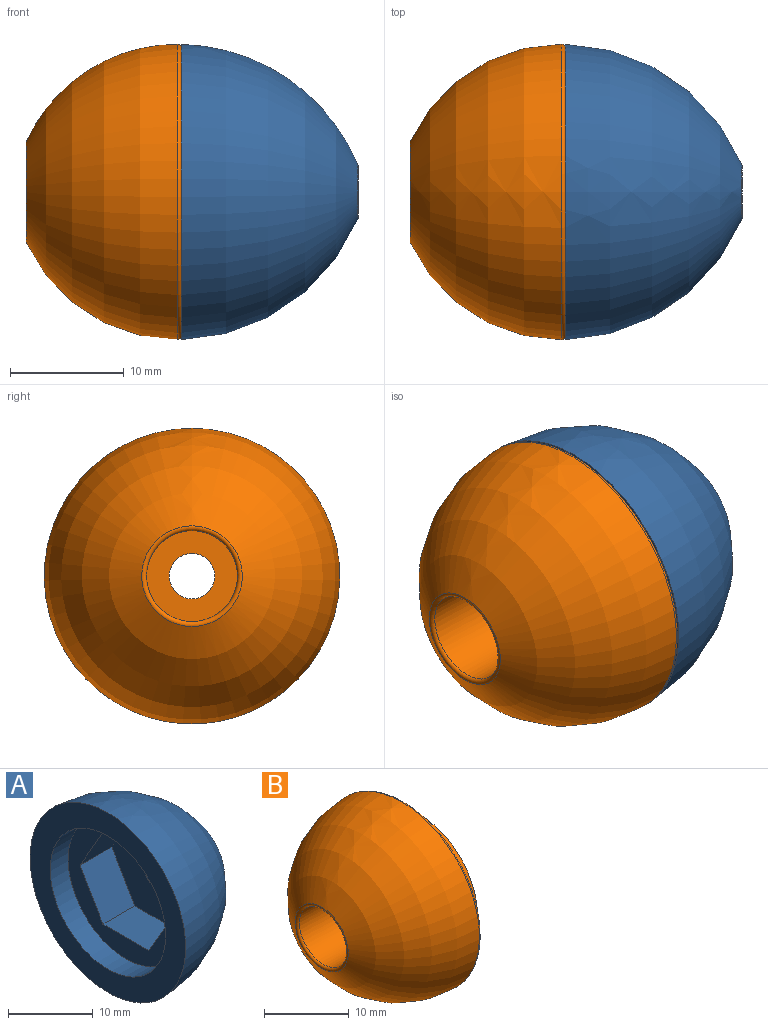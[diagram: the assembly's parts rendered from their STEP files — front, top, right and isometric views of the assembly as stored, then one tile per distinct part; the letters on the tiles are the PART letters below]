
ASSEMBLY  parts=2 mates=1
PART A: 14 faces, bbox 15.6x26x26 mm
  f0: plane 19.3x19.3mm, normal (-1,0,0), area 140.5mm2, adj f4,f8,f9,f10,f11,f12,f13
  f1: cylinder r=2mm len=6.66mm, axis (-1,0,0), area 83.6mm2, adj f6,f7
  f2: revolved ~26x26mm, area 2308.4mm2, adj f3,f6
  f3: plane 26x26mm, normal (-1,0,0), area 238.4mm2, adj f2,f4
  f4: cylinder r=9.65mm len=19.3mm, axis (-1,0,0), area 181.9mm2, adj f0,f3
  f5: plane 15.3x13.25mm, normal (-1,0,0), area 135.4mm2, adj f7,f8,f9,f10,f11,f12,f13
  f6: torus R=2.3mm, axis (1,0,0), area 8mm2, adj f1,f2
  f7: torus R=2.3mm, axis (1,0,0), area 6.2mm2, adj f1,f5
  f8: plane 6.63x5.3mm, normal (0,0.87,-0.5), area 40.5mm2, adj f0,f5,f9,f13
  f9: plane 7.65x5.3mm, normal (0,0,-1), area 40.5mm2, adj f0,f5,f8,f10
  f10: plane 6.63x5.3mm, normal (0,-0.87,-0.5), area 40.5mm2, adj f0,f5,f9,f11
  f11: plane 6.63x5.3mm, normal (0,-0.87,0.5), area 40.5mm2, adj f0,f5,f10,f12
  f12: plane 7.65x5.3mm, normal (0,0,1), area 40.5mm2, adj f0,f5,f11,f13
  f13: plane 6.63x5.3mm, normal (0,0.87,0.5), area 40.5mm2, adj f0,f5,f8,f12
PART B: 16 faces, bbox 16.5x28.2x28.2 mm
  f0: plane 19.1x19.1mm, normal (1,0,0), area 134.5mm2, adj f7,f8,f9,f10,f11,f12,f13
  f1: plane 25.41x25.41mm, normal (1,0,0), area 220.5mm2, adj f7,f14
  f2: revolved ~26.01x26.01mm, area 1055.9mm2, adj f14,f15
  f3: cylinder r=4mm len=8mm, axis (-1,0,0), area 148.6mm2, adj f4,f15
  f4: plane 8x8mm, normal (-1,0,0), area 37.7mm2, adj f3,f5
  f5: cylinder r=2mm len=4mm, axis (-1,0,0), area 15.7mm2, adj f4,f6
  f6: plane 15.05x14.41mm, normal (1,0,0), area 139.5mm2, adj f5,f8,f9,f10,f11,f12,f13
  f7: cylinder r=9.55mm len=19.1mm, axis (-1,0,0), area 168mm2, adj f0,f1
  f8: plane 9x5.83mm, normal (0,-0.65,-0.76), area 68.9mm2, adj f0,f6,f9,f13
  f9: plane 9x7.21mm, normal (0,0.34,-0.94), area 68.9mm2, adj f0,f6,f8,f10
  f10: plane 9x7.52mm, normal (0,0.98,-0.18), area 68.8mm2, adj f0,f6,f9,f11
  f11: plane 9x5.83mm, normal (0,0.65,0.76), area 68.9mm2, adj f0,f6,f10,f12
  f12: plane 9x7.21mm, normal (0,-0.34,0.94), area 68.9mm2, adj f0,f6,f11,f13
  f13: plane 9x7.52mm, normal (0,-0.98,0.18), area 68.9mm2, adj f0,f6,f8,f12
  f14: torus R=12.7mm, axis (-1,0,0), area 38.1mm2, adj f1,f2
  f15: torus R=4.3mm, axis (1,0,0), area 15.6mm2, adj f2,f3
PLACE A t=(-29.74,0,50.75)mm
PLACE B at identity
MATE planar A.f1 <-> B.f3  axis (-1,0,0) through (-42.41,0,50.65)mm
